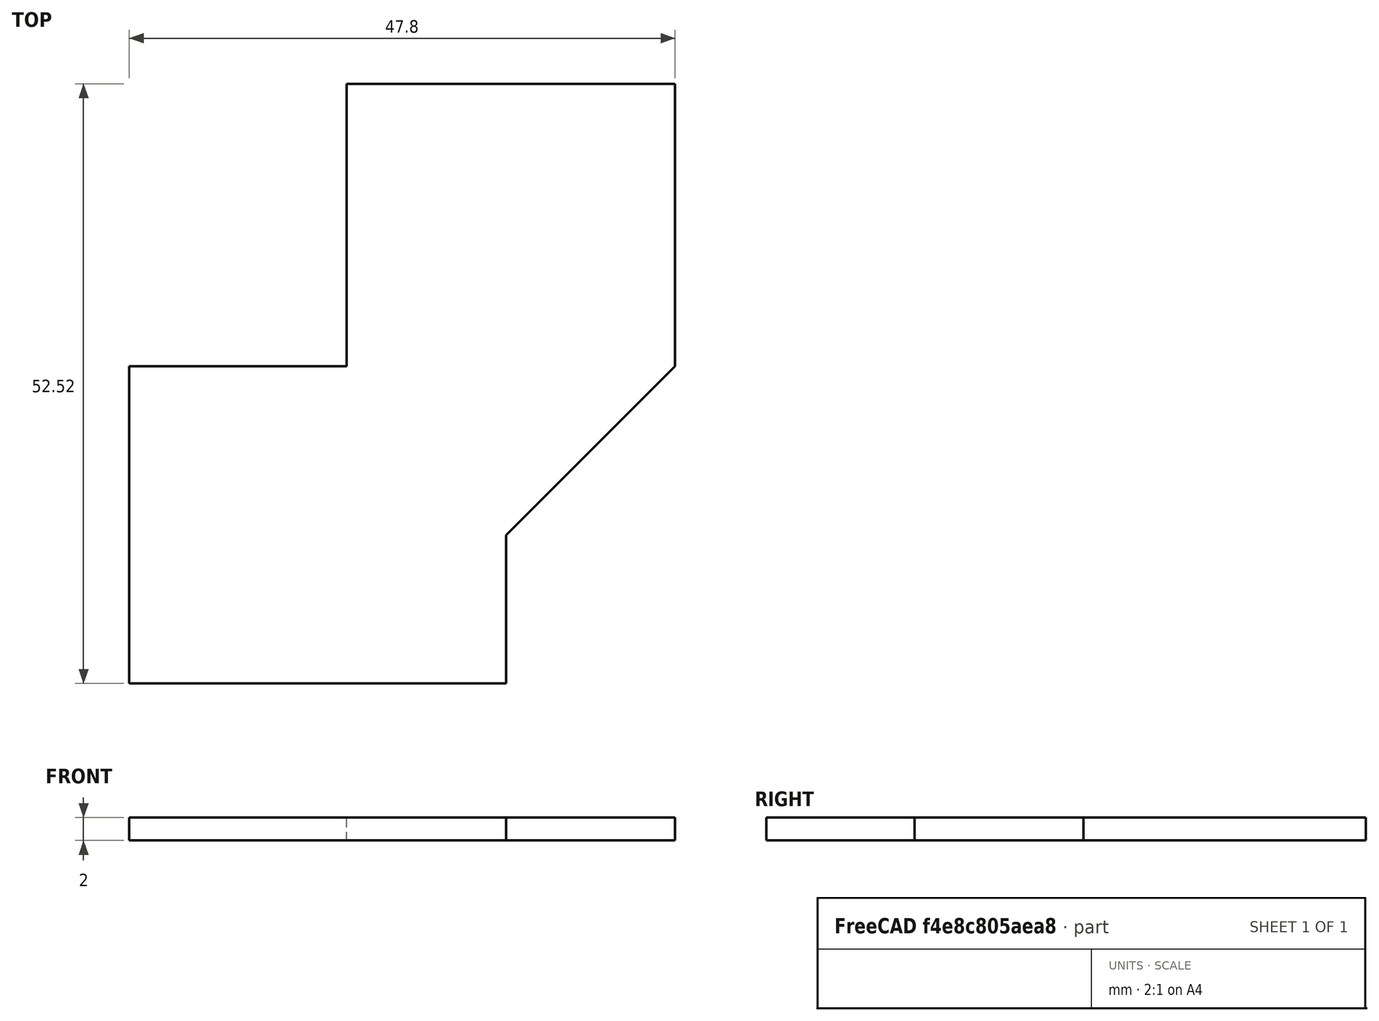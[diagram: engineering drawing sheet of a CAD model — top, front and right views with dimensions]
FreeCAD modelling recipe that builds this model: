
FCSTD DOCUMENT  (FreeCAD 0.20R29177 (Git))
Label: base
License: All rights reserved
LicenseURL: http://en.wikipedia.org/wiki/All_rights_reserved
objects: Sketcher::SketchObject×2, PartDesign::Pad×1, PartDesign::Body×1
note: 5 computed .brp shape members not serialized (recipe doc carries the construction recipe); baked Part::Feature solids carry a one-line shape summary decoded from their .brp

FEATURE [Sketcher::SketchObject] Sketch
  FullyConstrained = false
  MapMode = 5
  Support = -> [XY_Plane]
  sketch-geometry (9):
    g0: LineSegment StartX=-27.5845 StartY=6.31872 StartZ=0 EndX=-27.5845 EndY=-21.4813 EndZ=0
    g1: LineSegment StartX=-27.5845 StartY=-21.4813 StartZ=0 EndX=5.41553 EndY=-21.4813 EndZ=0
    g2: LineSegment StartX=5.41553 StartY=-21.4813 StartZ=0 EndX=5.41553 EndY=-8.48128 EndZ=0
    g3: LineSegment StartX=5.41553 StartY=-8.48128 StartZ=0 EndX=20.2155 EndY=6.31872 EndZ=0
    g4: LineSegment StartX=-27.5845 StartY=6.31872 StartZ=0 EndX=-8.53512 EndY=6.31872 EndZ=0
    g5: LineSegment StartX=-8.53512 StartY=6.31872 StartZ=0 EndX=-8.53512 EndY=31.0408 EndZ=0
    g6: LineSegment StartX=-8.53512 StartY=31.0408 StartZ=0 EndX=20.2155 EndY=31.0408 EndZ=0
    g7: LineSegment StartX=20.2155 StartY=31.0408 StartZ=0 EndX=20.2155 EndY=6.31872 EndZ=0
    g8: LineSegment StartX=20.2155 StartY=6.31872 StartZ=0 EndX=20.2155 EndY=-21.4813 EndZ=0
  constraints (23):
    c: Vertical(g0)
    c: Coincident(g0,g1)
    c: Horizontal(g1)
    c: Coincident(g1,g2)
    c: Coincident(g2,g3)
    c: Coincident(g0,g4)
    c: Horizontal(g4)
    c: Coincident(g4,g5)
    c: Vertical(g5)
    c: Coincident(g5,g6)
    c: Horizontal(g6)
    c: Coincident(g6,g7)
    c: Coincident(g7,g3)
    c: Distance(g1) = 33
    c: Distance(g0) = 27.8
    c: Vertical(g2)
    c: Angle(g2,g3) = 2.35619
    c: Vertical(g7)
    c: Coincident(g8,g3)
    c: Vertical(g8)
    c: Equal(g8,g0)
    c: Horizontal(g8,g1)
    c: Distance(g2) = 13
FEATURE [PartDesign::Pad] Pad
  Direction = (0,0,1)
  Length = 2
  Length2 = 10
  Profile = -> Sketch
  ReferenceAxis = -> Sketch [N_Axis]
  Type = 0
FEATURE [Sketcher::SketchObject] Sketch001
  FullyConstrained = true
  MapMode = 5
  Placement = pos=(0,0,2) rot=(0,0,1;0rad)
  Support = -> [Pad]
FEATURE [PartDesign::Body] Body  label="plate"
  Group = -> [Sketch,Pad,Sketch001]
  Origin = -> Origin
  Tip = -> Pad
